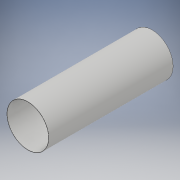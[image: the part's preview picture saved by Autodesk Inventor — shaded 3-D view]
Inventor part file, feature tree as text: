
AUTODESK INVENTOR PART (.ipt)
format: ipt  version: 2019 (Build 230136000, 136)  size: 100,864 bytes
history: native  units: mm
features: extrude x2, sketch x2
ambient origin geometry x8: Origin, YZ Plane, XZ Plane, XY Plane, X Axis, Y Axis, Z Axis, Center Point
bodies: Solid1 (feature_tree)
feature tree (4):
  extrude  "Extrusion1"  Depth=1200.0mm TaperAngle=0.0deg
  extrude  "Extrusion2"  Depth=120.0mm TaperAngle=0.0deg
  sketch  "Sketch1"  dims[d0=405.36mm d1=1200.0mm d2=0.0mm]
  sketch  "Sketch2"  dims[d3=400.0mm d4=120.0mm d5=0.0mm]
